# Revit family: Magnuson-Madison-Space_Divider_Connecting_Zipper-1
name_source: partatom
category: Furniture
revit_build: Autodesk Revit 2014 (Build: 20130308_1515(x64)
units: mm (PartAtom-declared; Revit-internal decimal feet)

## types (2) — shared parameters
Assembly Code = E2020200
Base Finish = MAG - Metal Black
Bracket Finish = MAG - Metal Black
Description = Freestanding space divider with acoustic fabric and connecting zipper feature
Keynote = 12500
Low Emitting Finish = Yes
Low Emitting Material = Yes
Manufacturer = Magnuson Group
Panel Back Finish = MAG - Fabric Ultramarine
Panel Front Finish = MAG - Fabric Ultramarine
Salvage or Reuse = Yes
Type Comments = Madison
URL = www.magnusongroup.com
Zipper Finish = MAG - Plastic Black
zero-valued in all types: Cost, Percentage of Recycled Content

## per-type parameters (varying)
| type | Depth | Height | Model | Width |
| MA-160-80-Z | 200 mm | 417 mm | MA-160-80-S-Z | 800 mm  [stored 2.62467 ft] |
| MA-160-100-Z | 290 mm  [stored 0.951444 ft] | 1650 mm  [stored 5.41339 ft] | MA-160-100-S-Z | 1000 mm  [stored 3.28084 ft] |

note: [stored X ft] marks values corroborated as IEEE doubles in the binary element streams (Revit-internal decimal feet)

## geometry (parser evidence)
native form markers: Sweep x1
no freeform markers — native parametric forms only
